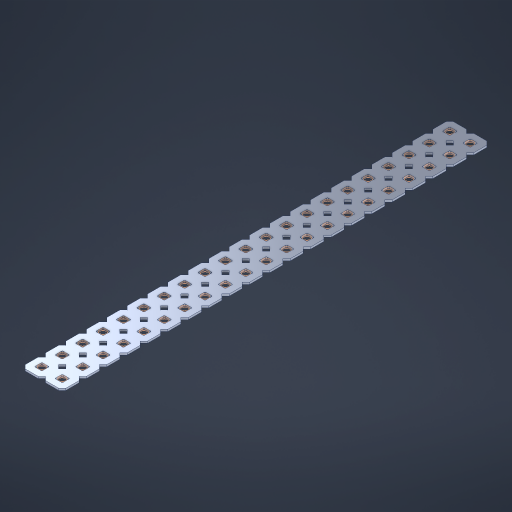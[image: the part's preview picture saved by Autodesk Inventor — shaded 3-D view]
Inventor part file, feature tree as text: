
AUTODESK INVENTOR PART (.ipt)
format: ipt  version: 2023 (Build 270158000, 158)  size: 740,352 bytes
history: native  units: in
note: dims shown in document units (in); Inventor stores cm internally (conversion verified against a paired STEP export)
features: other x43, extrude x41, sketch x2, pattern_linear x1
ambient origin geometry x8: Origin, YZ Plane, XZ Plane, XY Plane, X Axis, Y Axis, Z Axis, Center Point
bodies: Solid1 (feature_tree), Body (feature_tree)
feature tree (87):
  pattern_linear  "Rectangular Pattern1"  Spacing1=0.09in  [1 undecoded]
  sketch  "Sketch1"  dims[d1=0.5in]
  sketch  "Sketch2"  dims[d2=0.182in d3=0.09in d4=0.09in d5=0.09in d6=0.09in d7=0.09in d8=0.09in d9=0.09in d10=0.09in d11=0.02in d13=0.0in d14=0.172in d15=0.0625in d16=0.0in d19=0.5in d22=0.5in]
  other  "Srf1"
  other  "Srf126"
  other  "Srf127"
  other  "Srf128"
  other  "Srf129"
  other  "Srf130"
  other  "Srf131"
  other  "Srf250"
  other  "Srf251"
  other  "Srf252"
  other  "Srf253"
  other  "Srf254"
  other  "Srf255"
  other  "Srf256"
  other  "Srf257"
  other  "Srf258"
  other  "Srf259"
  other  "Srf260"
  other  "Srf261"
  other  "Srf262"
  other  "Srf263"
  other  "Srf268"
  other  "Srf269"
  other  "Srf270"
  other  "Srf271"
  other  "Srf272"
  other  "Srf273"
  other  "Srf274"
  other  "Srf275"
  other  "Srf276"
  other  "Srf277"
  other  "Srf278"
  other  "Srf279"
  other  "Srf280"
  other  "Srf281"
  other  "Srf282"
  other  "Srf283"
  other  "Srf284"
  other  "Srf285"
  other  "Srf286"
  other  "Srf287"
  other  "Srf288"
  other  "Circle"
  extrude  "ExtrusionSrf126"  Depth=0.09in
  extrude  "ExtrusionSrf127"  Depth=0.09in
  extrude  "ExtrusionSrf128"  Depth=0.09in
  extrude  "ExtrusionSrf129"  Depth=0.09in
  extrude  "ExtrusionSrf130"  Depth=0.09in
  extrude  "ExtrusionSrf131"  Depth=0.09in
  extrude  "ExtrusionSrf250"  Depth=0.09in
  extrude  "ExtrusionSrf251"  Depth=0.02in
  extrude  "ExtrusionSrf252"  TaperAngle=0.0deg  [1 undecoded]
  extrude  "ExtrusionSrf253"  Depth=0.5in
  extrude  "ExtrusionSrf254"  Depth=0.5in TaperAngle=0.0deg
  extrude  "ExtrusionSrf255"  Depth=0.5in
  extrude  "ExtrusionSrf256"  Depth=0.5in
  extrude  "ExtrusionSrf257"  [1 undecoded]
  extrude  "ExtrusionSrf258"  [1 undecoded]
  extrude  "ExtrusionSrf259"  [1 undecoded]
  extrude  "ExtrusionSrf260"  [1 undecoded]
  extrude  "ExtrusionSrf261"  [1 undecoded]
  extrude  "ExtrusionSrf262"  [1 undecoded]
  extrude  "ExtrusionSrf263"  [1 undecoded]
  extrude  "ExtrusionSrf268"  [1 undecoded]
  extrude  "ExtrusionSrf269"  [1 undecoded]
  extrude  "ExtrusionSrf270"  [1 undecoded]
  extrude  "ExtrusionSrf271"  [1 undecoded]
  extrude  "ExtrusionSrf272"  [1 undecoded]
  extrude  "ExtrusionSrf273"  [1 undecoded]
  extrude  "ExtrusionSrf274"  [1 undecoded]
  extrude  "ExtrusionSrf275"  [1 undecoded]
  extrude  "ExtrusionSrf276"  [1 undecoded]
  extrude  "ExtrusionSrf277"  [1 undecoded]
  extrude  "ExtrusionSrf278"  [1 undecoded]
  extrude  "ExtrusionSrf279"  [1 undecoded]
  extrude  "ExtrusionSrf280"  [1 undecoded]
  extrude  "ExtrusionSrf281"  [1 undecoded]
  extrude  "ExtrusionSrf282"  [1 undecoded]
  extrude  "ExtrusionSrf283"  [1 undecoded]
  extrude  "ExtrusionSrf284"  [1 undecoded]
  extrude  "ExtrusionSrf285"  [1 undecoded]
  extrude  "ExtrusionSrf286"  [1 undecoded]
  extrude  "ExtrusionSrf287"  [1 undecoded]
  extrude  "ExtrusionSrf288"  [1 undecoded]
note: 30 required parameter values undecoded (feature->parameter linkage not recoverable at this tier; creation-order binding heuristic only, values carry confidence <= 0.55)
